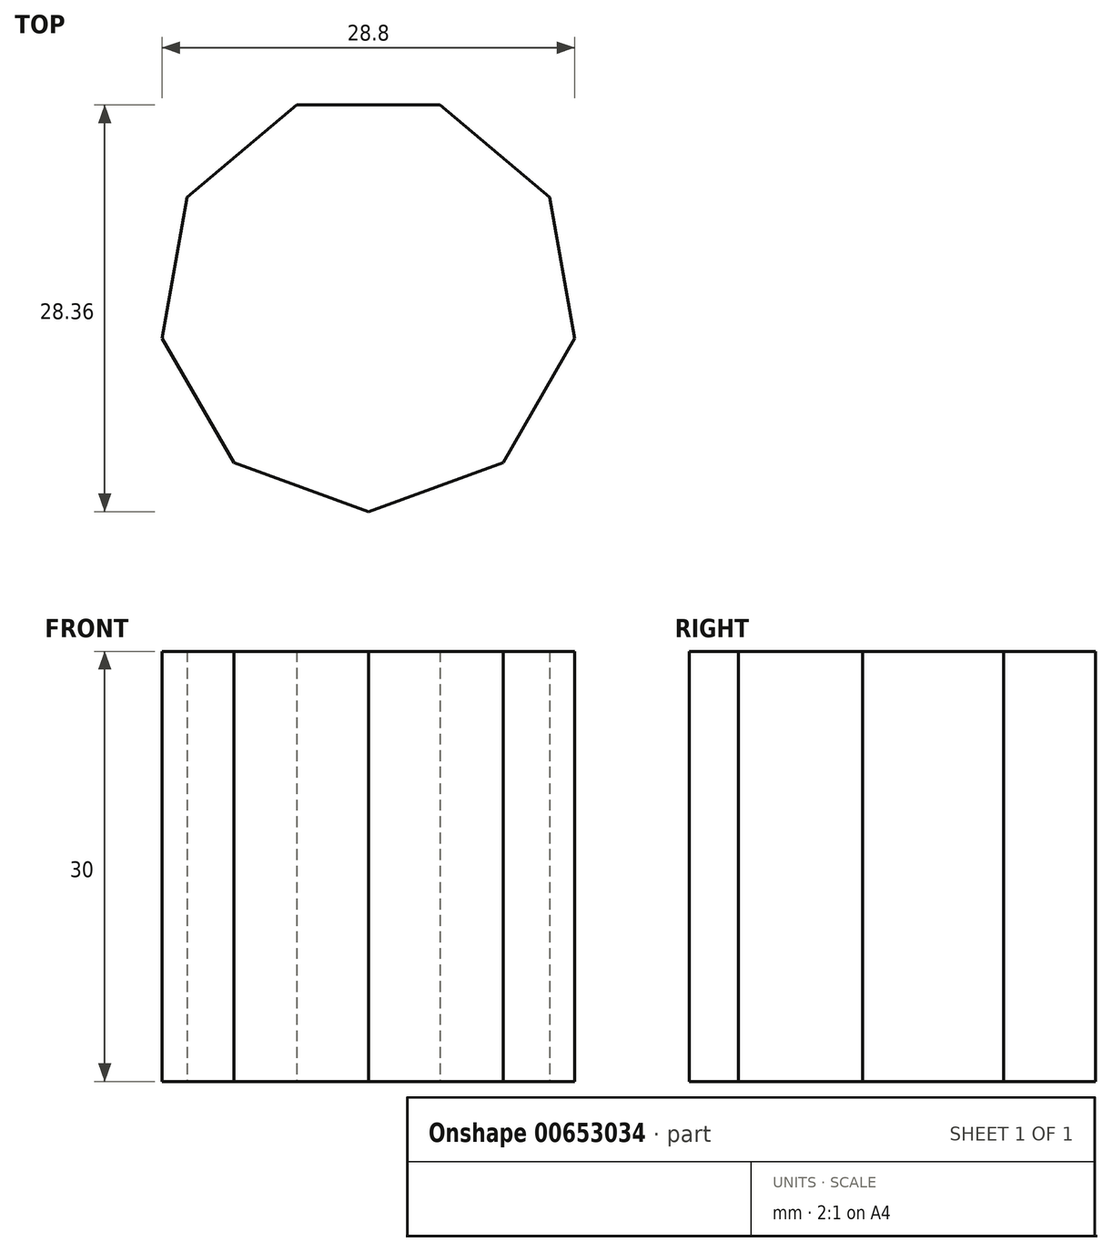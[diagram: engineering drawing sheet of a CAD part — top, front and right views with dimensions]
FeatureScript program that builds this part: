
annotation { "Feature Type Name" : "Feature", "Feature Type Description" : "" }
export const myFeature = defineFeature(function(context is Context, id is Id, definition is map)
    precondition{}
    {
        {
            var Q0;
            Q0=qCreatedBy(makeId("Top.planeOp"),FACE);
            var sketch = newSketch(context, id + "F0", { "sketchPlane" : qUnion([Q0])});
            skCircle(sketch, "E0.cCircle", {"center": v(0, 0) * mm, "radius": 13.74 * mm, "construction": true});
            skLineSegment(sketch, "E0.0", {"start": v(-5, 13.74) * mm, "end": v(5, 13.74) * mm});
            skLineSegment(sketch, "E0.1", {"start": v(5, 13.74) * mm, "end": v(12.66, 7.3) * mm});
            skLineSegment(sketch, "E0.2", {"start": v(12.66, 7.3) * mm, "end": v(14.4, -2.54) * mm});
            skLineSegment(sketch, "E0.3", {"start": v(14.4, -2.54) * mm, "end": v(9.4, -11.2) * mm});
            skLineSegment(sketch, "E0.4", {"start": v(9.4, -11.2) * mm, "end": v(0, -14.62) * mm});
            skLineSegment(sketch, "E0.5", {"start": v(0, -14.62) * mm, "end": v(-9.4, -11.2) * mm});
            skLineSegment(sketch, "E0.6", {"start": v(-9.4, -11.2) * mm, "end": v(-14.4, -2.54) * mm});
            skLineSegment(sketch, "E0.7", {"start": v(-14.4, -2.54) * mm, "end": v(-12.66, 7.3) * mm});
            skLineSegment(sketch, "E0.8", {"start": v(-12.66, 7.3) * mm, "end": v(-5, 13.74) * mm});
            skPoint(sketch, "E0.0.midPoint", {"position": v(0, 13.74) * mm});
            skSolve(sketch);
        }
        {
            var Q0;
            Q0 = qSketchRegion(id + "F0", true);
            extrude(context, id + "F1", {"entities" : qUnion([Q0]), "depth" : 30 * mm, "offsetDistance" : 25 * mm});
        }
    });
